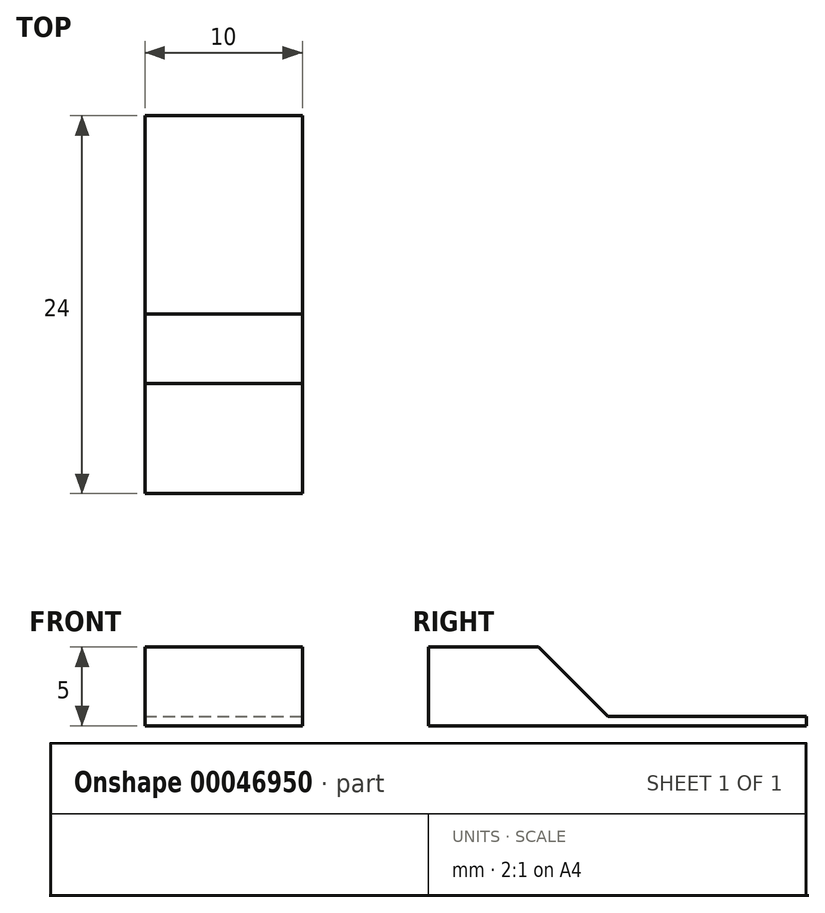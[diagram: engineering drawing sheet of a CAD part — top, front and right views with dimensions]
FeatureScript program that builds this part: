
annotation { "Feature Type Name" : "Feature", "Feature Type Description" : "" }
export const myFeature = defineFeature(function(context is Context, id is Id, definition is map)
    precondition{}
    {
        {
            var Q0;
            Q0=qCreatedBy(makeId("Top.planeOp"),FACE);
            var sketch = newSketch(context, id + "F0", { "sketchPlane" : qUnion([Q0])});
            skLineSegment(sketch, "E0.bottom", {"start": v(0, 0) * mm, "end": v(10, 0) * mm});
            skLineSegment(sketch, "E0.top", {"start": v(0, 10) * mm, "end": v(10, 10) * mm});
            skLineSegment(sketch, "E0.left", {"start": v(0, 0) * mm, "end": v(0, 10) * mm});
            skLineSegment(sketch, "E0.right", {"start": v(10, 0) * mm, "end": v(10, 10) * mm});
            skLineSegment(sketch, "E1.top", {"start": v(0, -2) * mm, "end": v(10, -2) * mm});
            skLineSegment(sketch, "E1.left", {"start": v(0, 0) * mm, "end": v(0, -2) * mm});
            skLineSegment(sketch, "E1.right", {"start": v(10, 0) * mm, "end": v(10, -2) * mm});
            skLineSegment(sketch, "E2.top", {"start": v(0, -14) * mm, "end": v(10, -14) * mm});
            skLineSegment(sketch, "E2.left", {"start": v(0, -2) * mm, "end": v(0, -14) * mm});
            skLineSegment(sketch, "E2.right", {"start": v(10, -2) * mm, "end": v(10, -14) * mm});
            skSolve(sketch);
        }
        {
            var Q0;
            Q0=makeQuery(id+"F0.imprint","IMPRINT",FACE,{"disambiguationData":[TD([[makeQuery(id+"F0.imprint","IMPRINT",EDGE,{"derivedFrom":sQuery(id+"F0.wireOp",EDGE,"E0.top")}),-1.0]])]});
            var Q1;
            Q1=makeQuery(id+"F0.imprint","IMPRINT",FACE,{"disambiguationData":[TD([[makeQuery(id+"F0.imprint","IMPRINT",EDGE,{"derivedFrom":sQuery(id+"F0.wireOp",EDGE,"E0.bottom")}),-1.0]])]});
            var Q2;
            Q2=makeQuery(id+"F0.imprint","IMPRINT",FACE,{"disambiguationData":[TD([[makeQuery(id+"F0.imprint","IMPRINT",EDGE,{"derivedFrom":sQuery(id+"F0.wireOp",EDGE,"E1.top")}),-1.0]])]});
            extrude(context, id + "F1", {"entities" : qUnion([Q0, Q1, Q2]), "depth" : 0.6 * mm});
        }
        {
            var Q0;
            Q0=makeQuery(id+"F0.imprint","IMPRINT",FACE,{"disambiguationData":[TD([[makeQuery(id+"F0.imprint","IMPRINT",EDGE,{"derivedFrom":sQuery(id+"F0.wireOp",EDGE,"E1.top")}),-1.0]])]});
            extrude(context, id + "F2", {"entities" : qUnion([Q0]), "operationType" : NewBodyOperationType.ADD, "depth" : 5 * mm});
        }
        {
            var Q0;
            Q0=makeQuery(id+"F2.opExtrude","CAP_EDGE",EDGE,{"disambiguationData":[OSD([sQuery(id+"F0.wireOp",EDGE,"E1.top")])],"isStart":false});
            chamfer(context, id + "F3", {"entities" : qUnion([Q0]), "width" : 5 * mm, "tangentPropagation" : true});
        }
    });
